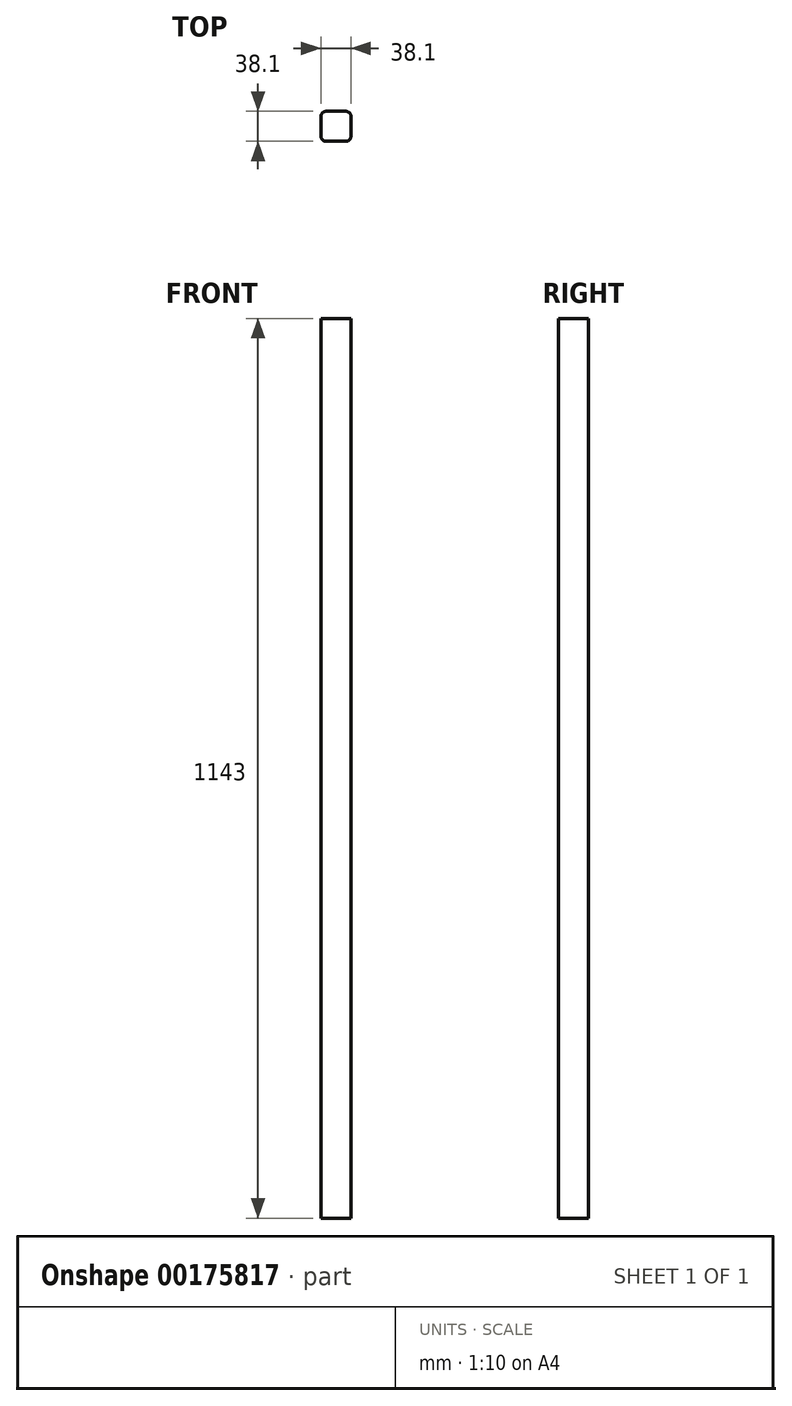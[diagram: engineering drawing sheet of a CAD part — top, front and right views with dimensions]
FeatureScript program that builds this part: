
annotation { "Feature Type Name" : "Feature", "Feature Type Description" : "" }
export const myFeature = defineFeature(function(context is Context, id is Id, definition is map)
    precondition{}
    {
        {
            var Q0;
            Q0=qCreatedBy(makeId("Top.planeOp"),FACE);
            var sketch = newSketch(context, id + "F0", { "sketchPlane" : qUnion([Q0])});
            skLineSegment(sketch, "E0.bottom", {"start": v(12.7, 19.05) * mm, "end": v(-12.7, 19.05) * mm});
            skLineSegment(sketch, "E0.top", {"start": v(12.7, -19.05) * mm, "end": v(-12.7, -19.05) * mm});
            skLineSegment(sketch, "E0.left", {"start": v(19.05, 12.7) * mm, "end": v(19.05, -12.7) * mm});
            skLineSegment(sketch, "E0.right", {"start": v(-19.05, 12.7) * mm, "end": v(-19.05, -12.7) * mm});
            skPoint(sketch, "E0.middle", {"position": v(0, 0) * mm});
            skPoint(sketch, "E1.visualSharp", {"position": v(-19.05, 19.05) * mm});
            skArc(sketch, "E1.filletArc", {"start": v(-12.7, 19.05) * mm, "mid": v(-17.2, 17.2) * mm, "end": v(-19.05, 12.7) * mm});
            skPoint(sketch, "E2.visualSharp", {"position": v(19.05, 19.05) * mm});
            skArc(sketch, "E2.filletArc", {"start": v(19.05, 12.7) * mm, "mid": v(17.2, 17.2) * mm, "end": v(12.7, 19.05) * mm});
            skPoint(sketch, "E3.visualSharp", {"position": v(19.05, -19.05) * mm});
            skArc(sketch, "E3.filletArc", {"start": v(12.7, -19.05) * mm, "mid": v(17.2, -17.2) * mm, "end": v(19.05, -12.7) * mm});
            skPoint(sketch, "E4.visualSharp", {"position": v(-19.05, -19.05) * mm});
            skArc(sketch, "E4.filletArc", {"start": v(-19.05, -12.7) * mm, "mid": v(-17.2, -17.2) * mm, "end": v(-12.7, -19.05) * mm});
            skSolve(sketch);
        }
        {
            var Q0;
            Q0=qSketchRegion(id+"F0",true);
            extrude(context, id + "F1", {"entities" : qUnion([Q0]), "depth" : 1143 * mm, "offsetDistance" : 25.4 * mm});
        }
    });
